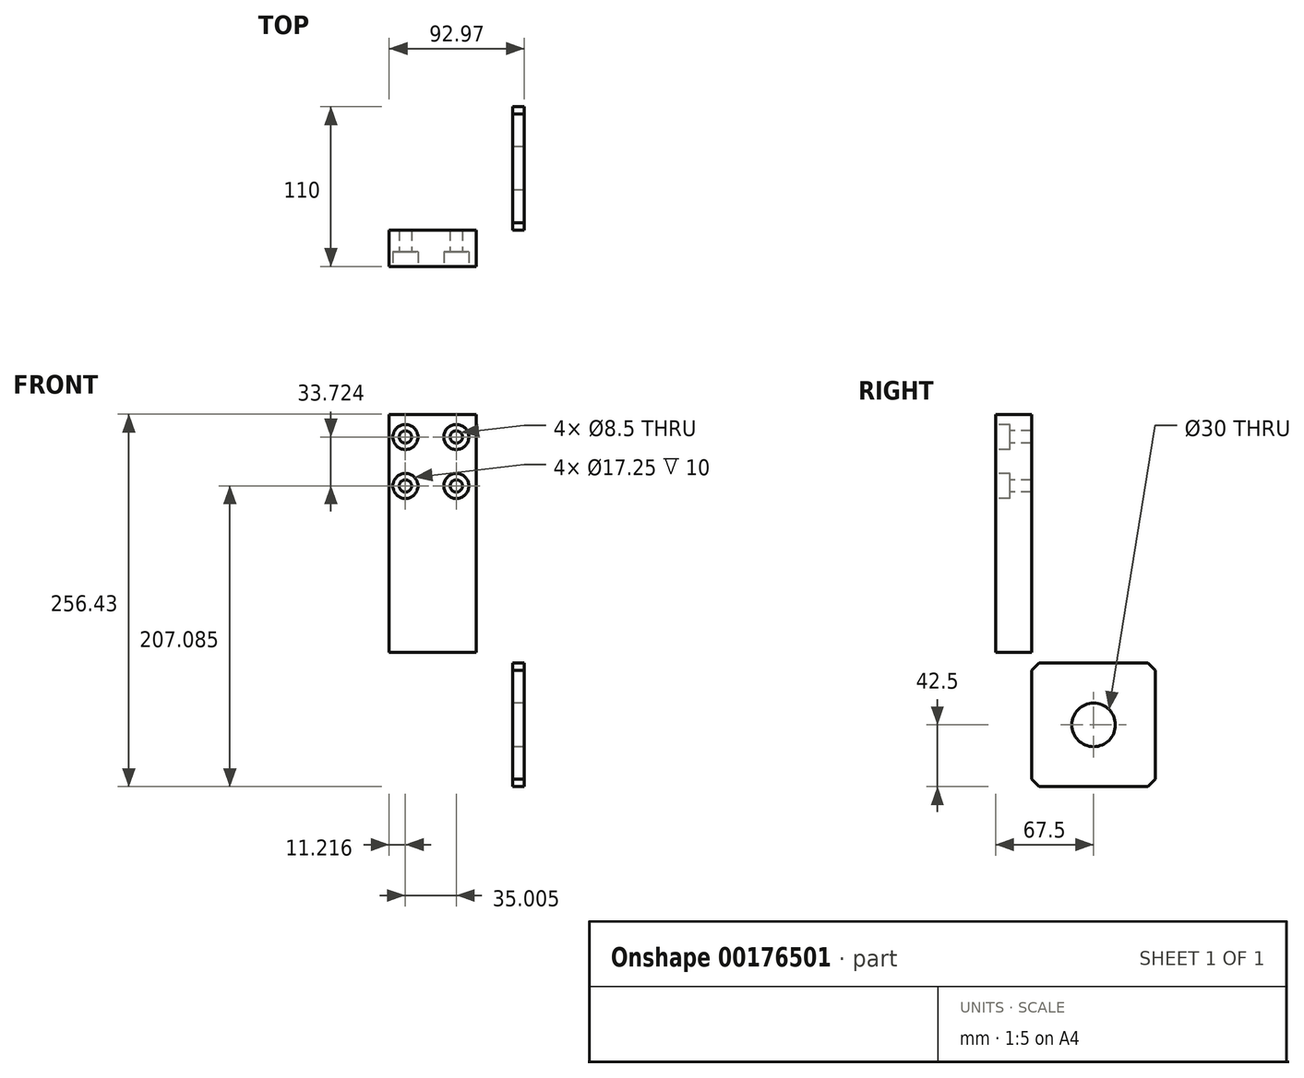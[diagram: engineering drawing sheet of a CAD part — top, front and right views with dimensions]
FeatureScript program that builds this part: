
annotation { "Feature Type Name" : "Feature", "Feature Type Description" : "" }
export const myFeature = defineFeature(function(context is Context, id is Id, definition is map)
    precondition{}
    {
        {
            var Q0;
            Q0=qCreatedBy(makeId("Right.planeOp"),FACE);
            var sketch = newSketch(context, id + "F0", { "sketchPlane" : qUnion([Q0])});
            skLineSegment(sketch, "E0.bottom", {"start": v(0, 0) * mm, "end": v(85, 0) * mm});
            skLineSegment(sketch, "E0.top", {"start": v(0, -85) * mm, "end": v(85, -85) * mm});
            skLineSegment(sketch, "E0.left", {"start": v(0, 0) * mm, "end": v(0, -85) * mm});
            skLineSegment(sketch, "E0.right", {"start": v(85, 0) * mm, "end": v(85, -85) * mm});
            skLineSegment(sketch, "E1", {"start": v(0, 0) * mm, "end": v(85, -85) * mm, "construction": true});
            skLineSegment(sketch, "E2", {"start": v(0, -85) * mm, "end": v(85, 0) * mm, "construction": true});
            skCircle(sketch, "E3", {"center": v(42.5, -42.5) * mm, "radius": 15 * mm});
            skLineSegment(sketch, "E4", {"start": v(-5.52, -8) * mm, "end": v(99.14, -8) * mm, "construction": true});
            skLineSegment(sketch, "E5", {"start": v(-7.18, -81) * mm, "end": v(94.82, -81) * mm, "construction": true});
            skLineSegment(sketch, "E6", {"start": v(7.86, 5.68) * mm, "end": v(7.86, -95.2) * mm, "construction": true});
            skLineSegment(sketch, "E7", {"start": v(0, -49.14) * mm, "end": v(7.86, -49.14) * mm, "construction": true});
            skLineSegment(sketch, "E8", {"start": v(77.14, 8.22) * mm, "end": v(77.14, -107.63) * mm, "construction": true});
            skSolve(sketch);
        }
        {
            var Q0;
            Q0=makeQuery(id+"F0.imprint","IMPRINT",FACE,{"disambiguationData":[TD([[makeQuery(id+"F0.imprint","IMPRINT",EDGE,{"derivedFrom":sQuery(id+"F0.wireOp",EDGE,"E0.bottom")}),-1.0]])]});
            extrude(context, id + "F1", {"entities" : qUnion([Q0]), "depth" : 8 * mm});
        }
        {
            var Q0;
            Q0=makeQuery(id+"F1.opExtrude","SWEPT_EDGE",EDGE,{"disambiguationData":[OSD([sQuery(id+"F0.wireOp",EDGE,"E0.bottom"),sQuery(id+"F0.wireOp",EDGE,"E0.right")])]});
            chamfer(context, id + "F2", {"entities" : qUnion([Q0]), "width" : 5 * mm, "tangentPropagation" : true});
        }
        {
            var Q0;
            Q0=makeQuery(id+"F1.opExtrude","SWEPT_EDGE",EDGE,{"disambiguationData":[OSD([sQuery(id+"F0.wireOp",EDGE,"E0.bottom"),sQuery(id+"F0.wireOp",EDGE,"E0.left")])]});
            var Q1;
            Q1=makeQuery(id+"F1.opExtrude","SWEPT_EDGE",EDGE,{"disambiguationData":[OSD([sQuery(id+"F0.wireOp",EDGE,"E0.top"),sQuery(id+"F0.wireOp",EDGE,"E0.left")])]});
            var Q2;
            Q2=makeQuery(id+"F1.opExtrude","SWEPT_EDGE",EDGE,{"disambiguationData":[OSD([sQuery(id+"F0.wireOp",EDGE,"E0.top"),sQuery(id+"F0.wireOp",EDGE,"E0.right")])]});
            chamfer(context, id + "F3", {"entities" : qUnion([Q0, Q1, Q2]), "width" : 5 * mm, "tangentPropagation" : true});
        }
        {
            var Q0;
            Q0=qCreatedBy(makeId("Front.planeOp"),FACE);
            var sketch = newSketch(context, id + "F4", { "sketchPlane" : qUnion([Q0])});
            skLineSegment(sketch, "E9.bottom", {"start": v(-84.97, 171.43) * mm, "end": v(-24.97, 171.43) * mm});
            skLineSegment(sketch, "E9.top", {"start": v(-84.97, 7.43) * mm, "end": v(-24.97, 7.43) * mm});
            skLineSegment(sketch, "E9.left", {"start": v(-84.97, 171.43) * mm, "end": v(-84.97, 7.43) * mm});
            skLineSegment(sketch, "E9.right", {"start": v(-24.97, 171.43) * mm, "end": v(-24.97, 7.43) * mm});
            skPoint(sketch, "E10", {"position": v(-72.59, 151.16) * mm});
            skPoint(sketch, "E11", {"position": v(-46.96, 151.16) * mm});
            skSolve(sketch);
        }
        {
            var Q0;
            Q0 = qSketchRegion(id + "F4", true);
            extrude(context, id + "F5", {"entities" : qUnion([Q0]), "depth" : 25 * mm});
        }
        {
            var Q0;
            Q0=makeQuery(id+"F5.opExtrude","CAP_FACE",FACE,{"disambiguationData":[OSD([sQuery(id+"F4.wireOp",EDGE,"E9.bottom"),sQuery(id+"F4.wireOp",EDGE,"E9.top"),sQuery(id+"F4.wireOp",EDGE,"E9.left"),sQuery(id+"F4.wireOp",EDGE,"E9.right")])],"isStart":false});
            var sketch = newSketch(context, id + "F6", { "sketchPlane" : qUnion([Q0])});
            skPoint(sketch, "E12", {"position": v(-73.75, 155.8) * mm});
            skPoint(sketch, "E13", {"position": v(-38.75, 155.8) * mm});
            skPoint(sketch, "E14", {"position": v(-73.75, 122.09) * mm});
            skPoint(sketch, "E15", {"position": v(-38.75, 122.09) * mm});
            skSolve(sketch);
        }
        {
            var Q0;
            Q0=sQuery(id+"F6.wireOp",VERTEX,"E12");
            var Q1;
            Q1=sQuery(id+"F6.wireOp",VERTEX,"E13");
            var Q2;
            Q2=sQuery(id+"F6.wireOp",VERTEX,"E15");
            var Q3;
            Q3=sQuery(id+"F6.wireOp",VERTEX,"E14");
            var Q4;
            Q4=makeQuery(id+"F5.opExtrude","SWEPT_BODY",BODY,{"disambiguationData":[OSD([sQuery(id+"F4.wireOp",EDGE,"E9.bottom"),sQuery(id+"F4.wireOp",EDGE,"E9.top"),sQuery(id+"F4.wireOp",EDGE,"E9.left"),sQuery(id+"F4.wireOp",EDGE,"E9.right")])]});
            hole(context, id + "F7", {"style" : HoleStyle.C_BORE, "endStyle" : HoleEndStyle.THROUGH, "standardTappedOrClearance" : lookupTablePath({ "standard" : "ISO", "engagement" : "75%", "pitch" : "1.5 mm", "size" : "M10", "type" : "Tapped" }), "standardBlindInLast" : lookupTablePath({ "standard" : "ISO", "engagement" : "75%", "pitch" : "1.5 mm", "size" : "M10", "type" : "Tapped" }), "holeDiameter" : 8.5 * mm, "cBoreDiameter" : 17.25 * mm, "cBoreDepth" : 10 * mm, "startFromSketch" : true, "locations" : qUnion([Q0, Q1, Q2, Q3]), "scope" : qUnion([Q4]), "isTappedThrough" : true, "majorDiameter" : 10 * mm, "showTappedDepth" : true});
        }
    });
